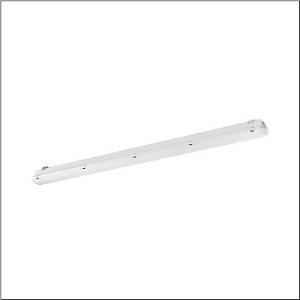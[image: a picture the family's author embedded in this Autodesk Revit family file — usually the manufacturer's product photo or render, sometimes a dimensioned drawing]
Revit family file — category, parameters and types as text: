
# Revit family: monsun_r__11xtreme_mo_51fe10dp460m_82e5
name_source: partatom
category: Lighting Fixtures
units: mm (PartAtom-declared; Revit-internal decimal feet)

## family parameters
Cut with Voids When Loaded = No
Host = Face
Light Source = No
Part Type = Normal
Room Calculation Point = No
Round Connector Dimension = Use Diameter
Shared = No

## types (1)
- --- (1 x LED, 6370 lm, 34.5 W, 4000K)
    Apparent Load = 35 VA
    CIE Flux Codes = 47 77 93 94 100
    Color Rendering = 80
    Color Temperature = 4000K
    Default Elevation = 1800 mm
    Description = Monsun® 11Xtreme MO, damp-proof luminaire, chain hanger, primary optical cover: enclosure, of PMMA, light emission: direct distribution, primary light characteristic: symmetric, installation type: suspended mounting, surface-mounted, horizontal mounting, vertical mounting, LED, rated luminous flux: 6.370lm, luminous efficacy: 185lm/W, light colour: 840, colour temperature: 4000K, control gear: DALI 2, with terminal, 5-pole, max. 2.5mm², mains connection: 220..240V, AC, 50/60Hz, rated input power: 35W, luminaire housing, of glass-fibre reinforced polyester, uncoated, bright grey, incl. chain hanger, length: 1.590mm, width: 90mm, height: 88mm, clip for enclosure, of stainless steel (V2A), ceiling mounting element, of stainless steel (V2A), chain hanger, of stainless steel (V2A), protection rating (complete): IP66, insulation class (complete): insulation class I (protective earthing), certification: CE, ENEC, VDE, UKCA, protection symbol: D, impact resistance: IK04, permissible operating ambient temperature: -35..+55°C, standard: EN 50419, EN 60598-2-1, contact your sales advisor before using the luminaires in applications with unclear chemical exposure, large temperature fluctuations or condensation-forming humidity, LABS conformity tested according to VDMA 24364:2018-05, no direct snow, no direct sun, no direct rain, for indoor or canopied outdoor use, corresponds to IFS (International Featured Standards) requirements for safety and quality in the food industry, packaging unit: 1 piece
    Height = 88 mm
    Lamp = 1 x LED
    Lamp Light Flux = 6370 lm
    Lamp Power = 34.5 W
    Lamp count = 1
    Length = 1590 mm
    Luminous efficacy = 185 lm/W
    Manufacturer = Siteco
    ModVariant = No
    Model = 51FE10DP460M
    Mounting Place = Ceiling
    Mounting Type = Surface mounted
    Number of Poles = 1
    OnlyDefault = Yes
    Power Factor = 1
    Product Name = Monsun® 11Xtreme MO
    Product group = damp-proof luminaire
    ProductGroupID = 301
    Protection Class = Protection class I
    Protection Degree = IP 66
    RLX_Detail_Level = 1
    RLX_Emergency_Light_Flux = 0 lm
    RLX_Emergency_Type = 0
    RLX_Emergency_Type_DB = No
    RlxData = <blob elided: 87073 chars, md5=e583d99a>
    Socket = socket
    Standby Power = 0 W
    System Light Flux = 6370 lm
    System Power = 35 W
    Type Comments = factory setting: luminous flux: 100 % | dim-lin: 254 | 231 mA
    Type Image = l_1349234.jpg
    URL = http://relux.com
    VarID = @adj_037665
    Voltage = 0 V
    Weight = 0.00 kg
    Width = 90 mm

## geometry (parser evidence)
native form markers: Blend x4, Sweep x13
no freeform markers — native parametric forms only
